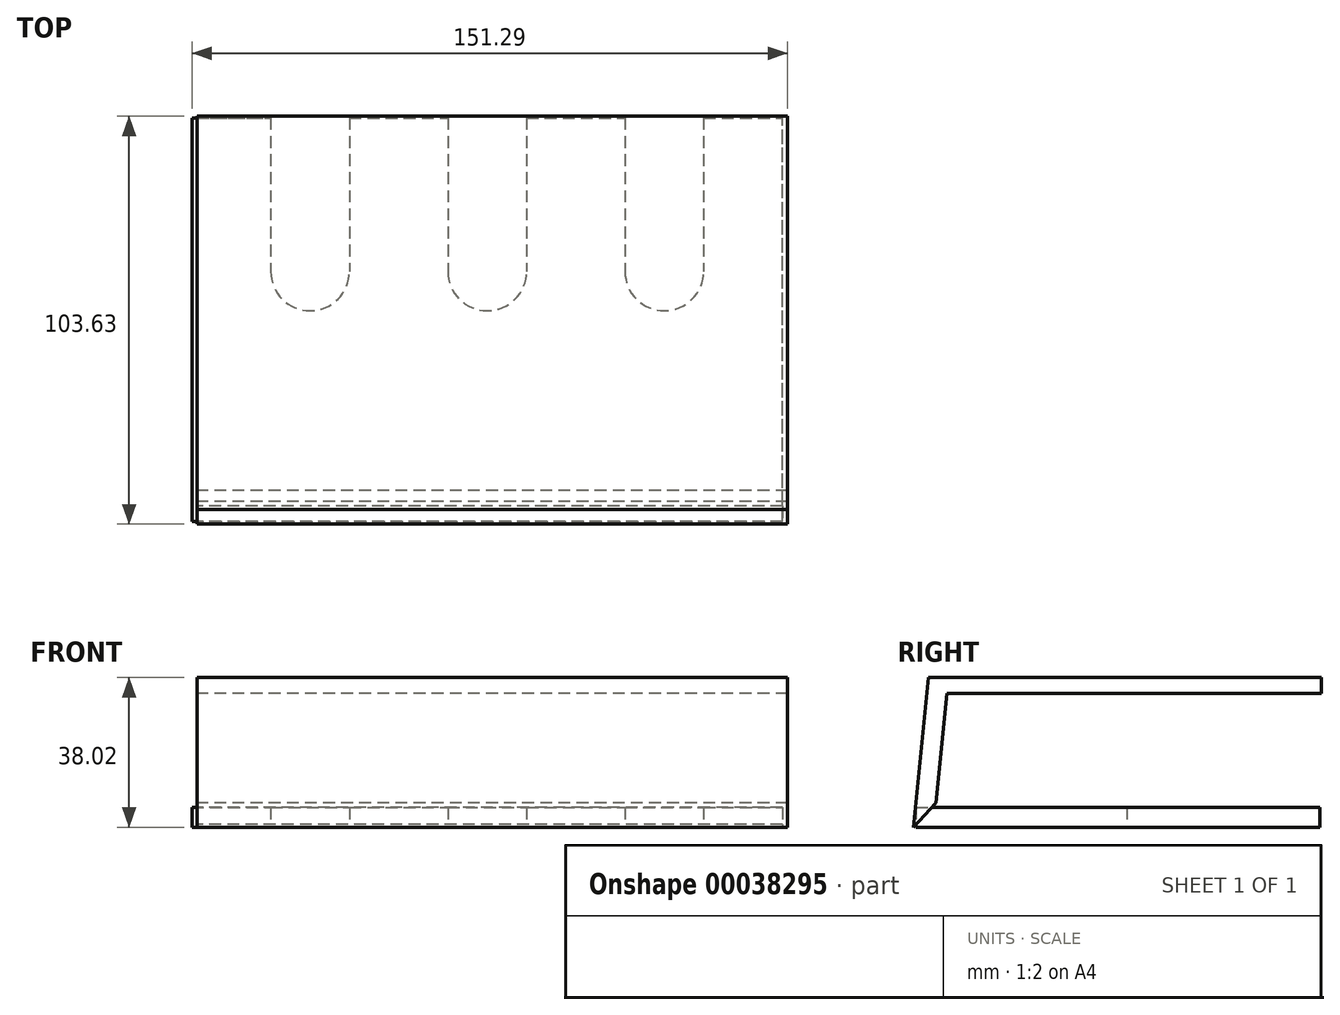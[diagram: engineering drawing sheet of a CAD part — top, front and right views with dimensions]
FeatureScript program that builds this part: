
annotation { "Feature Type Name" : "Feature", "Feature Type Description" : "" }
export const myFeature = defineFeature(function(context is Context, id is Id, definition is map)
    precondition{}
    {
        {
            var Q0;
            Q0=qCreatedBy(makeId("Top.planeOp"),FACE);
            var sketch = newSketch(context, id + "F0", { "sketchPlane" : qUnion([Q0])});
            skLineSegment(sketch, "E0.bottom", {"start": v(-76.3, -63.57) * mm, "end": v(73.7, -63.57) * mm});
            skLineSegment(sketch, "E0.top", {"start": v(-76.3, 38.97) * mm, "end": v(-56.3, 38.97) * mm});
            skLineSegment(sketch, "E0.left", {"start": v(-76.3, -63.57) * mm, "end": v(-76.3, 38.97) * mm});
            skLineSegment(sketch, "E0.right", {"start": v(73.7, -63.57) * mm, "end": v(73.7, 38.97) * mm});
            skLineSegment(sketch, "E1", {"start": v(-56.3, 38.97) * mm, "end": v(-56.3, 0) * mm});
            skLineSegment(sketch, "E2", {"start": v(-36.3, 38.97) * mm, "end": v(-36.3, 0) * mm});
            skLineSegment(sketch, "E3", {"start": v(-11.3, 38.97) * mm, "end": v(-11.3, 0) * mm});
            skLineSegment(sketch, "E4", {"start": v(8.7, 38.97) * mm, "end": v(8.7, 0) * mm});
            skLineSegment(sketch, "E5", {"start": v(33.7, 38.97) * mm, "end": v(33.7, 0) * mm});
            skLineSegment(sketch, "E6", {"start": v(53.7, 38.97) * mm, "end": v(53.7, 0) * mm});
            skArc(sketch, "E7", {"start": v(-56.3, 0) * mm, "mid": v(-46.3, -10) * mm, "end": v(-36.3, 0) * mm});
            skArc(sketch, "E8", {"start": v(-11.3, 0) * mm, "mid": v(-1.3, -10) * mm, "end": v(8.7, 0) * mm});
            skArc(sketch, "E9", {"start": v(33.7, 0) * mm, "mid": v(43.7, -10) * mm, "end": v(53.7, 0) * mm});
            skLineSegment(sketch, "E10.trimOffspring", {"start": v(-36.3, 38.97) * mm, "end": v(-11.3, 38.97) * mm});
            skLineSegment(sketch, "E11.trimOffspring", {"start": v(8.7, 38.97) * mm, "end": v(33.7, 38.97) * mm});
            skLineSegment(sketch, "E12.trimOffspring", {"start": v(53.7, 38.97) * mm, "end": v(73.7, 38.97) * mm});
            skSolve(sketch);
        }
        {
            var Q0;
            Q0 = qSketchRegion(id + "F0", true);
            extrude(context, id + "F1", {"entities" : qUnion([Q0]), "depth" : 5 * mm});
        }
        {
            var Q0;
            Q0=qCreatedBy(makeId("Right.planeOp"),FACE);
            var sketch = newSketch(context, id + "F2", { "sketchPlane" : qUnion([Q0])});
            skLineSegment(sketch, "E13", {"start": v(-64.22, 0) * mm, "end": v(-60.45, 38.02) * mm});
            skLineSegment(sketch, "E14", {"start": v(-60.45, 38.02) * mm, "end": v(39.4, 38.02) * mm});
            skLineSegment(sketch, "E15", {"start": v(39.4, 38.02) * mm, "end": v(39.4, 34.05) * mm});
            skLineSegment(sketch, "E16", {"start": v(39.4, 34.05) * mm, "end": v(-55.68, 34.05) * mm});
            skLineSegment(sketch, "E17", {"start": v(-55.68, 34.05) * mm, "end": v(-58.46, 6.25) * mm});
            skLineSegment(sketch, "E18", {"start": v(-58.46, 6.25) * mm, "end": v(-64.22, 0) * mm});
            skSolve(sketch);
        }
        {
            var Q0;
            Q0 = qSketchRegion(id + "F2", true);
            extrude(context, id + "F3", {"entities" : qUnion([Q0]), "operationType" : NewBodyOperationType.ADD, "endBound" : BoundingType.SYMMETRIC, "depth" : 150 * mm});
        }
    });
